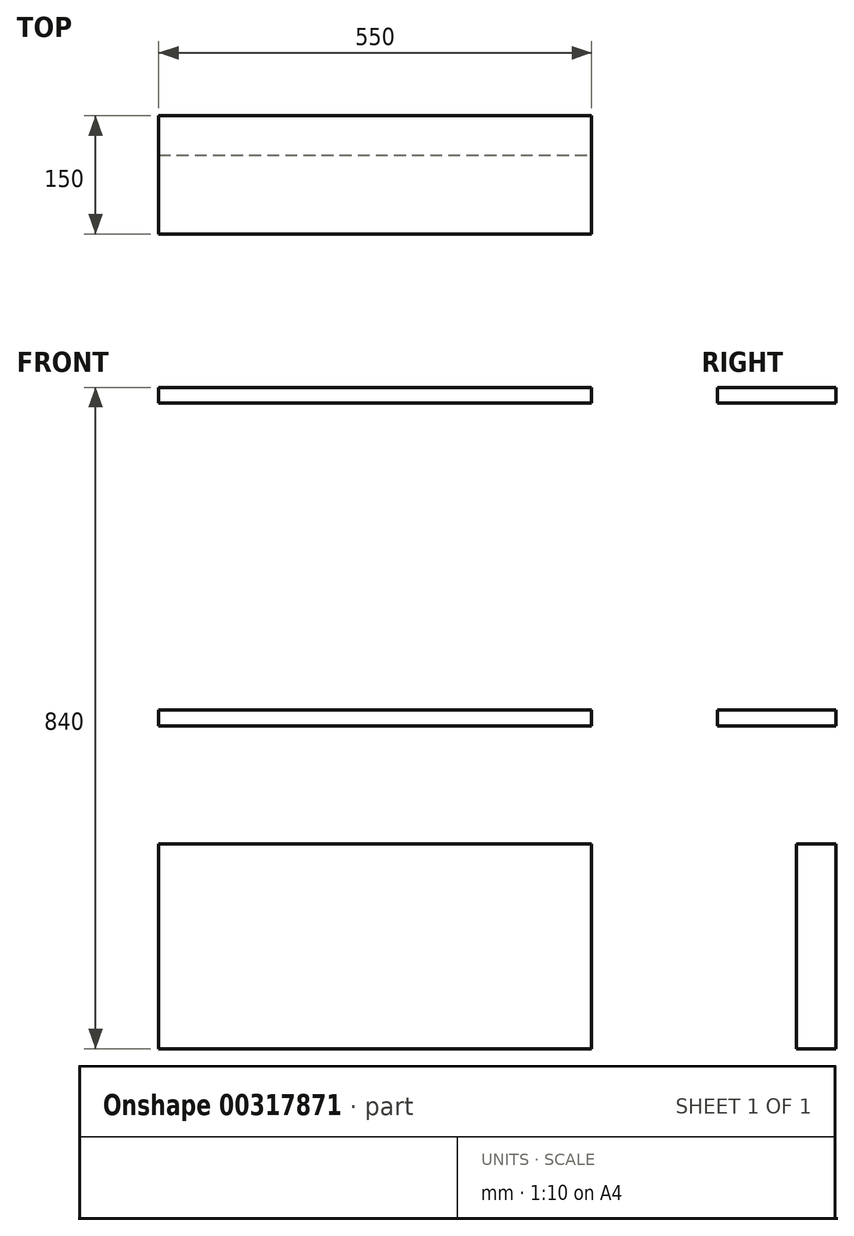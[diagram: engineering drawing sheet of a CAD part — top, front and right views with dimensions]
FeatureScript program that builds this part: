
annotation { "Feature Type Name" : "Feature", "Feature Type Description" : "" }
export const myFeature = defineFeature(function(context is Context, id is Id, definition is map)
    precondition{}
    {
        {
            var Q0;
            Q0=qCreatedBy(makeId("Front.planeOp"),FACE);
            var sketch = newSketch(context, id + "F0", { "sketchPlane" : qUnion([Q0])});
            skLineSegment(sketch, "E0.bottom", {"start": v(-275, 450) * mm, "end": v(275, 450) * mm});
            skLineSegment(sketch, "E0.top", {"start": v(-275, -450) * mm, "end": v(275, -450) * mm});
            skLineSegment(sketch, "E0.left", {"start": v(-275, 450) * mm, "end": v(-275, -450) * mm});
            skLineSegment(sketch, "E0.right", {"start": v(275, 450) * mm, "end": v(275, -450) * mm});
            skPoint(sketch, "E0.middle", {"position": v(0, 0) * mm});
            skLineSegment(sketch, "E1.bottom", {"start": v(-275, 20) * mm, "end": v(275, 20) * mm});
            skLineSegment(sketch, "E1.top", {"start": v(-275, 40) * mm, "end": v(275, 40) * mm});
            skLineSegment(sketch, "E1.left", {"start": v(-275, 20) * mm, "end": v(-275, 40) * mm});
            skLineSegment(sketch, "E1.right", {"start": v(275, 20) * mm, "end": v(275, 40) * mm});
            skLineSegment(sketch, "E2.top", {"start": v(-275, -390) * mm, "end": v(275, -390) * mm});
            skLineSegment(sketch, "E2.left", {"start": v(-275, -450) * mm, "end": v(-275, -390) * mm});
            skLineSegment(sketch, "E2.right", {"start": v(275, -450) * mm, "end": v(275, -390) * mm});
            skLineSegment(sketch, "E3.top", {"start": v(-275, -130) * mm, "end": v(275, -130) * mm});
            skLineSegment(sketch, "E3.left", {"start": v(-275, -450) * mm, "end": v(-275, -130) * mm});
            skLineSegment(sketch, "E3.right", {"start": v(275, -450) * mm, "end": v(275, -130) * mm});
            skLineSegment(sketch, "E4.top", {"start": v(-275, 430) * mm, "end": v(275, 430) * mm});
            skLineSegment(sketch, "E4.left", {"start": v(-275, 450) * mm, "end": v(-275, 430) * mm});
            skLineSegment(sketch, "E4.right", {"start": v(275, 450) * mm, "end": v(275, 430) * mm});
            skLineSegment(sketch, "E5.left", {"start": v(-275, -390) * mm, "end": v(-275, -450) * mm});
            skLineSegment(sketch, "E5.right", {"start": v(275, -390) * mm, "end": v(275, -450) * mm});
            skSolve(sketch);
        }
        {
            var Q0;
            Q0=makeQuery(id+"F0.imprint","IMPRINT",FACE,{"disambiguationData":[TD([[makeQuery(id+"F0.imprint","IMPRINT",EDGE,{"derivedFrom":sQuery(id+"F0.wireOp",EDGE,"E0.bottom")}),-1.0]])]});
            var Q1;
            Q1=makeQuery(id+"F0.imprint","IMPRINT",FACE,{"disambiguationData":[TD([[makeQuery(id+"F0.imprint","IMPRINT",EDGE,{"derivedFrom":sQuery(id+"F0.wireOp",EDGE,"E1.bottom")}),1.0]])]});
            extrude(context, id + "F1", {"entities" : qUnion([Q0, Q1]), "depth" : 150 * mm});
        }
        {
            var Q0;
            Q0=makeQuery(id+"F0.imprint","IMPRINT",FACE,{"disambiguationData":[TD([[makeQuery(id+"F0.imprint","IMPRINT",EDGE,{"derivedFrom":sQuery(id+"F0.wireOp",EDGE,"E3.top")}),-1.0]])]});
            extrude(context, id + "F2", {"entities" : qUnion([Q0]), "depth" : 50 * mm});
        }
    });
